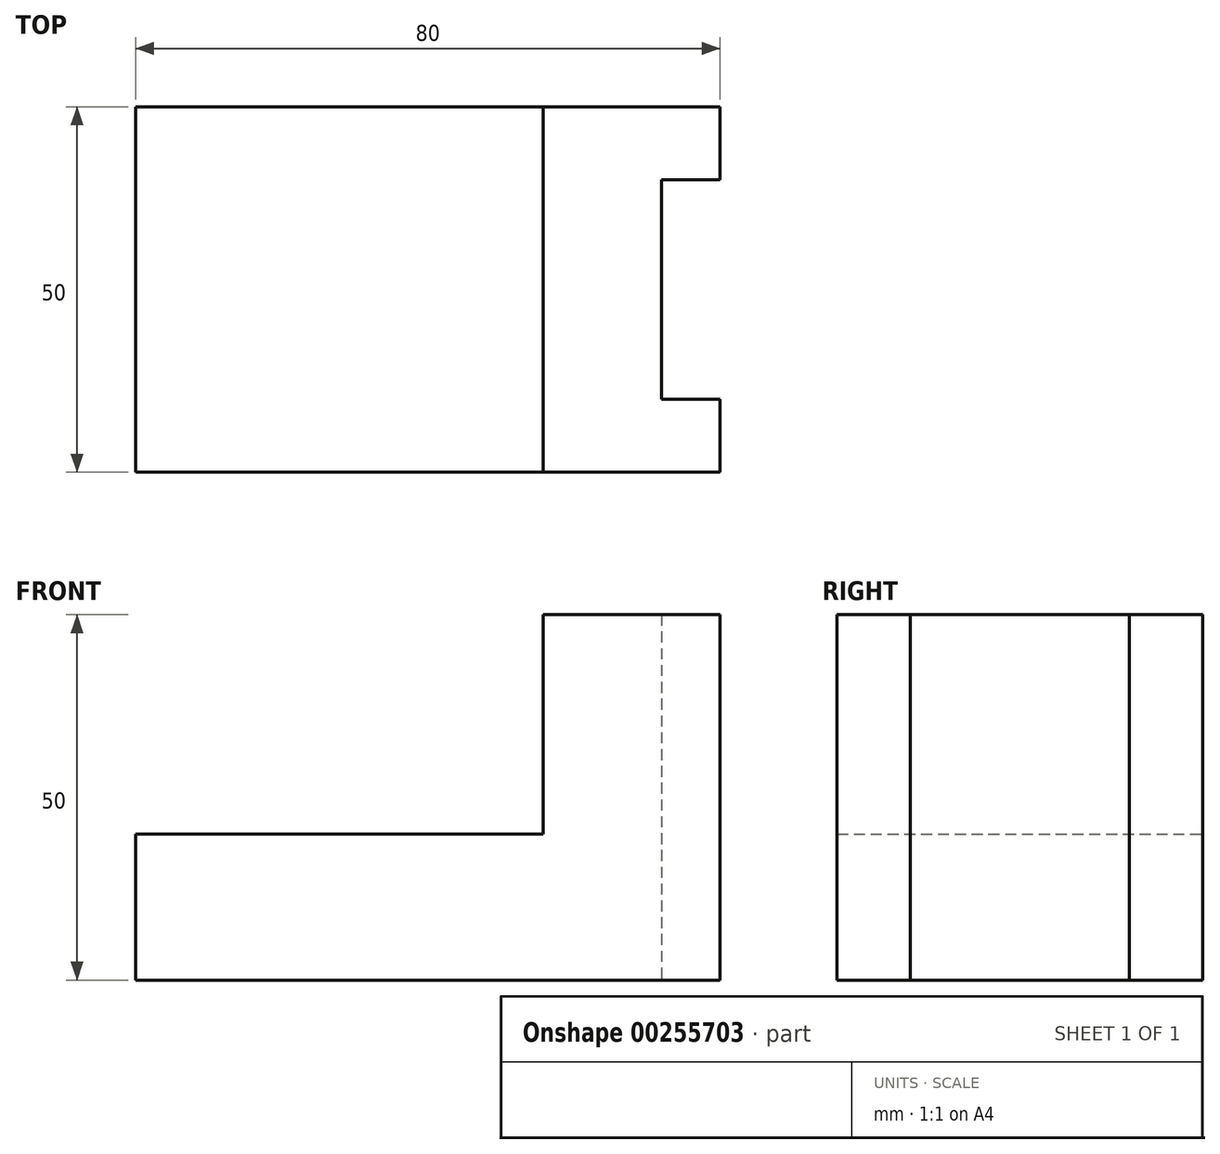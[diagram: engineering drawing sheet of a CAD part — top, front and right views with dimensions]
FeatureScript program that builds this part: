
annotation { "Feature Type Name" : "Feature", "Feature Type Description" : "" }
export const myFeature = defineFeature(function(context is Context, id is Id, definition is map)
    precondition{}
    {
        {
            var Q0;
            Q0=qCreatedBy(makeId("Top.planeOp"),FACE);
            var sketch = newSketch(context, id + "F0", { "sketchPlane" : qUnion([Q0])});
            skLineSegment(sketch, "E0.bottom", {"start": v(0, 0) * mm, "end": v(55.8, 0) * mm});
            skLineSegment(sketch, "E0.top", {"start": v(0, 50) * mm, "end": v(55.8, 50) * mm});
            skLineSegment(sketch, "E0.left", {"start": v(0, 0) * mm, "end": v(0, 50) * mm});
            skLineSegment(sketch, "E0.right", {"start": v(55.8, 0) * mm, "end": v(55.8, 50) * mm});
            skLineSegment(sketch, "E1.bottom", {"start": v(55.8, 50) * mm, "end": v(80, 50) * mm});
            skLineSegment(sketch, "E1.top", {"start": v(55.8, 0) * mm, "end": v(80, 0) * mm});
            skLineSegment(sketch, "E1.left", {"start": v(55.8, 50) * mm, "end": v(55.8, 0) * mm});
            skLineSegment(sketch, "E1.right", {"start": v(80, 50) * mm, "end": v(80, 0) * mm});
            skLineSegment(sketch, "E2.bottom", {"start": v(80, 40) * mm, "end": v(72, 40) * mm});
            skLineSegment(sketch, "E2.top", {"start": v(80, 10) * mm, "end": v(72, 10) * mm});
            skLineSegment(sketch, "E2.left", {"start": v(80, 40) * mm, "end": v(80, 10) * mm});
            skLineSegment(sketch, "E2.right", {"start": v(72, 40) * mm, "end": v(72, 10) * mm});
            skSolve(sketch);
        }
        {
            var Q0;
            Q0=makeQuery(id+"F0.imprint","IMPRINT",FACE,{"disambiguationData":[TD([[makeQuery(id+"F0.imprint","IMPRINT",EDGE,{"derivedFrom":sQuery(id+"F0.wireOp",EDGE,"E0.bottom")}),1.0]])]});
            extrude(context, id + "F1", {"entities" : qUnion([Q0]), "depth" : 20 * mm});
        }
        {
            var Q0;
            {var subQ1=sQuery(id+"F0.wireOp",EDGE,"E1.bottom");Q0=makeQuery(id+"F0.imprint","IMPRINT",FACE,{"disambiguationData":[TD([[makeQuery(id+"F0.imprint","IMPRINT",EDGE,{"derivedFrom":subQ1}),-1.0]])]});}
            extrude(context, id + "F2", {"entities" : qUnion([Q0]), "operationType" : NewBodyOperationType.ADD, "depth" : 50 * mm});
        }
    });
